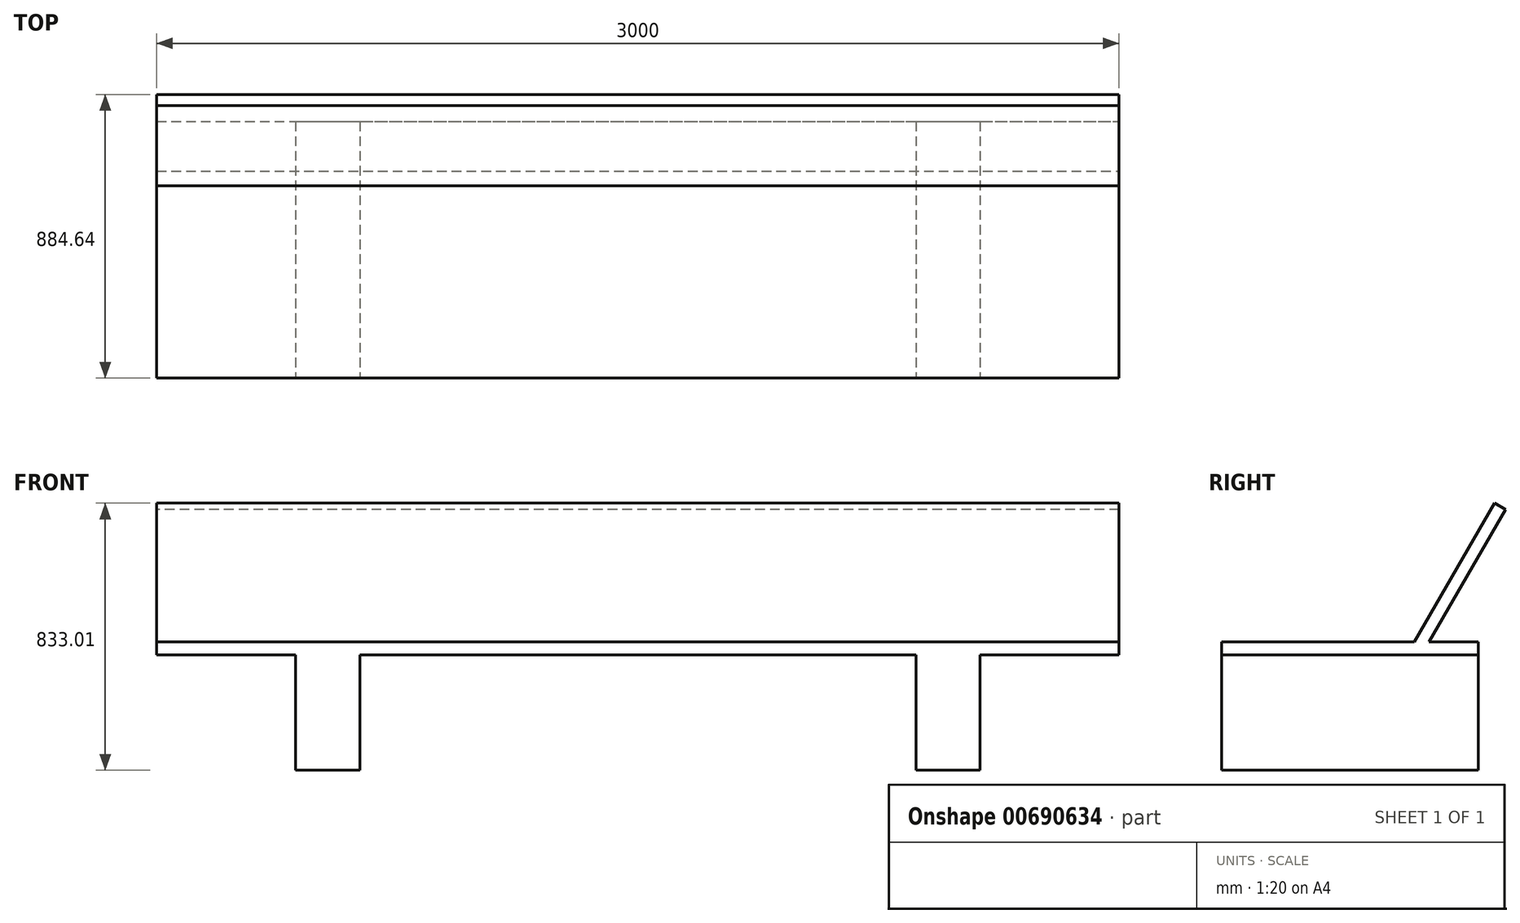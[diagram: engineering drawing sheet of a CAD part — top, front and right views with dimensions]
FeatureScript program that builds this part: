
annotation { "Feature Type Name" : "Feature", "Feature Type Description" : "" }
export const myFeature = defineFeature(function(context is Context, id is Id, definition is map)
    precondition{}
    {
        {
            var Q0;
            Q0=qCreatedBy(makeId("Top.planeOp"),FACE);
            var sketch = newSketch(context, id + "F0", { "sketchPlane" : qUnion([Q0])});
            skLineSegment(sketch, "E0.bottom", {"start": v(0, 0) * mm, "end": v(3000, 0) * mm});
            skLineSegment(sketch, "E0.top", {"start": v(0, -800) * mm, "end": v(3000, -800) * mm});
            skLineSegment(sketch, "E0.left", {"start": v(0, 0) * mm, "end": v(0, -800) * mm});
            skLineSegment(sketch, "E0.right", {"start": v(3000, 0) * mm, "end": v(3000, -800) * mm});
            skSolve(sketch);
        }
        {
            var Q0;
            Q0 = qSketchRegion(id + "F0", true);
            extrude(context, id + "F1", {"entities" : qUnion([Q0]), "depth" : 40 * mm, "offsetDistance" : 25 * mm});
        }
        {
            var Q0;
            Q0=makeQuery(id+"F1.opExtrude","CAP_FACE",FACE,{"disambiguationData":[OSD([sQuery(id+"F0.wireOp",EDGE,"E0.bottom"),sQuery(id+"F0.wireOp",EDGE,"E0.top"),sQuery(id+"F0.wireOp",EDGE,"E0.left"),sQuery(id+"F0.wireOp",EDGE,"E0.right")])],"isStart":false});
            var sketch = newSketch(context, id + "F2", { "sketchPlane" : qUnion([Q0])});
            skLineSegment(sketch, "E1.bottom", {"start": v(633.02, 0) * mm, "end": v(433.02, 0) * mm});
            skLineSegment(sketch, "E1.top", {"start": v(633.02, -800) * mm, "end": v(433.02, -800) * mm});
            skLineSegment(sketch, "E1.left", {"start": v(633.02, 0) * mm, "end": v(633.02, -800) * mm});
            skLineSegment(sketch, "E1.right", {"start": v(433.02, 0) * mm, "end": v(433.02, -800) * mm});
            skLineSegment(sketch, "E2.bottom", {"start": v(2366.98, 0) * mm, "end": v(2566.98, 0) * mm});
            skLineSegment(sketch, "E2.top", {"start": v(2366.98, -800) * mm, "end": v(2566.98, -800) * mm});
            skLineSegment(sketch, "E2.left", {"start": v(2366.98, 0) * mm, "end": v(2366.98, -800) * mm});
            skLineSegment(sketch, "E2.right", {"start": v(2566.98, 0) * mm, "end": v(2566.98, -800) * mm});
            skLineSegment(sketch, "E3", {"start": v(0, -400) * mm, "end": v(433.02, -400) * mm, "construction": true});
            skLineSegment(sketch, "E4", {"start": v(433.02, -400) * mm, "end": v(2566.98, -400) * mm, "construction": true});
            skLineSegment(sketch, "E5", {"start": v(2566.98, -400) * mm, "end": v(3000, -400) * mm, "construction": true});
            skSolve(sketch);
        }
        {
            var Q0;
            Q0 = qSketchRegion(id + "F2", true);
            extrude(context, id + "F3", {"entities" : qUnion([Q0]), "operationType" : NewBodyOperationType.ADD, "oppositeDirection" : true, "depth" : 400 * mm, "offsetDistance" : 25 * mm});
        }
        {
            var Q0;
            Q0=qCreatedBy(makeId("Right.planeOp"),FACE);
            var sketch = newSketch(context, id + "F4", { "sketchPlane" : qUnion([Q0])});
            skLineSegment(sketch, "E6", {"start": v(84.64, 453.01) * mm, "end": v(50, 473.01) * mm});
            skLineSegment(sketch, "E7", {"start": v(50, 473.01) * mm, "end": v(-200, 40) * mm});
            skLineSegment(sketch, "E8", {"start": v(-200, 40) * mm, "end": v(-165.36, 20) * mm});
            skLineSegment(sketch, "E9", {"start": v(-165.36, 20) * mm, "end": v(84.64, 453.01) * mm});
            skLineSegment(sketch, "E10", {"start": v(-182.68, 30) * mm, "end": v(-200, 0) * mm, "construction": true});
            skSolve(sketch);
        }
        {
            var Q0;
            Q0 = qSketchRegion(id + "F4", true);
            var Q1;
            Q1=makeQuery(id+"F1.opExtrude","SWEPT_FACE",FACE,{"disambiguationData":[OSD([sQuery(id+"F0.wireOp",EDGE,"E0.right")])]});
            extrude(context, id + "F5", {"entities" : qUnion([Q0]), "operationType" : NewBodyOperationType.ADD, "endBound" : BoundingType.UP_TO_SURFACE, "depth" : 25 * mm, "endBoundEntityFace" : qUnion([Q1]), "offsetDistance" : 25 * mm});
        }
    });
